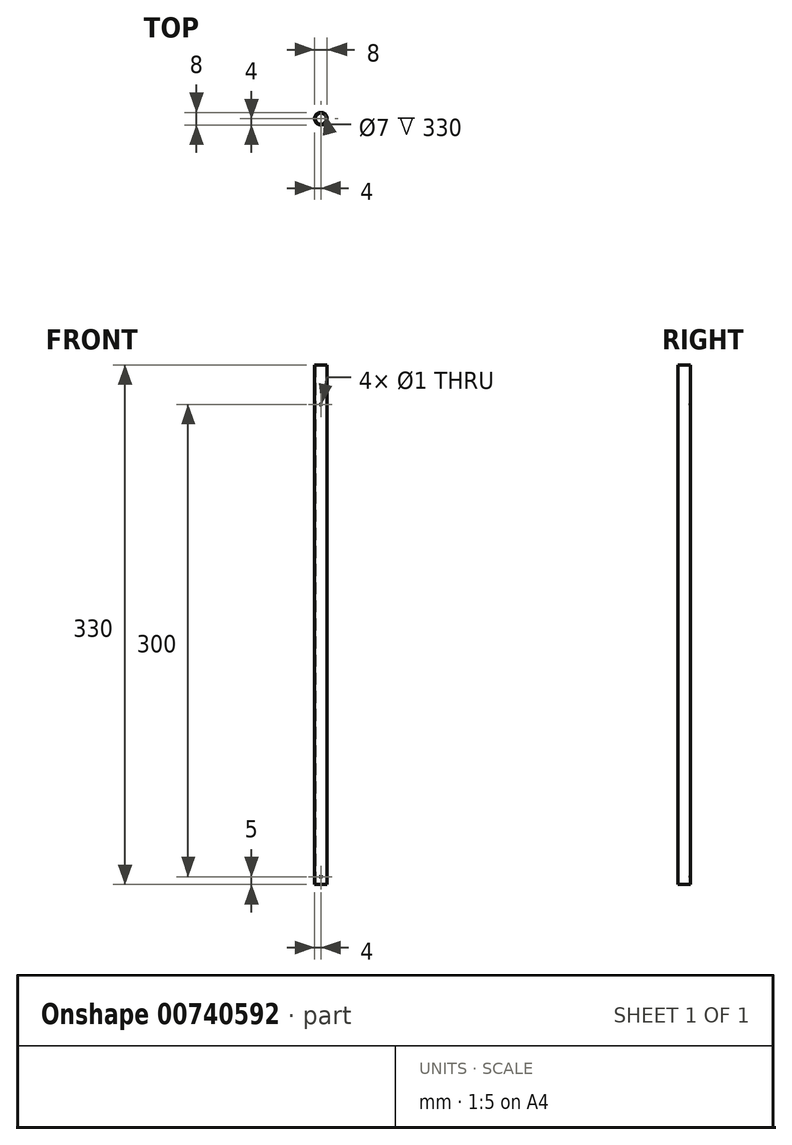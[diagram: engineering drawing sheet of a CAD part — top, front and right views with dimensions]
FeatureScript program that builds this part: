
annotation { "Feature Type Name" : "Feature", "Feature Type Description" : "" }
export const myFeature = defineFeature(function(context is Context, id is Id, definition is map)
    precondition{}
    {
        {
            var Q0;
            Q0=qCreatedBy(makeId("Top.planeOp"),FACE);
            var sketch = newSketch(context, id + "F0", { "sketchPlane" : qUnion([Q0])});
            skCircle(sketch, "E0", {"center": v(0, 0) * mm, "radius": 4 * mm});
            skCircle(sketch, "E1", {"center": v(0, 0) * mm, "radius": 3.5 * mm});
            skSolve(sketch);
        }
        {
            var Q0;
            Q0=makeQuery(id+"F0.imprint","IMPRINT",FACE,{"disambiguationData":[TD([[makeQuery(id+"F0.imprint","IMPRINT",EDGE,{"derivedFrom":sQuery(id+"F0.wireOp",EDGE,"E0")}),1.0]])]});
            extrude(context, id + "F1", {"entities" : qUnion([Q0]), "depth" : 330 * mm, "offsetDistance" : 25 * mm});
        }
        {
            var Q0;
            Q0=qCreatedBy(makeId("Front.planeOp"),FACE);
            var sketch = newSketch(context, id + "F2", { "sketchPlane" : qUnion([Q0])});
            skCircle(sketch, "E2", {"center": v(0, 5) * mm, "radius": 0.5 * mm});
            skCircle(sketch, "E3", {"center": v(0, 305) * mm, "radius": 0.5 * mm});
            skSolve(sketch);
        }
        {
            var Q0;
            Q0 = qSketchRegion(id + "F2", true);
            extrude(context, id + "F3", {"entities" : qUnion([Q0]), "operationType" : NewBodyOperationType.REMOVE, "endBound" : BoundingType.THROUGH_ALL, "oppositeDirection" : true, "depth" : 25 * mm, "offsetDistance" : 25 * mm, "hasSecondDirection" : true, "secondDirectionOppositeDirection" : false, "secondDirectionDepth" : 25 * mm});
        }
    });
